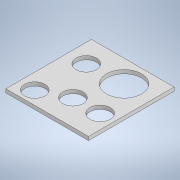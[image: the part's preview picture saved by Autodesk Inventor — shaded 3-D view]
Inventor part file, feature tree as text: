
AUTODESK INVENTOR PART (.ipt)
format: ipt  version: 2021 (Build 250183000, 183)  size: 131,584 bytes
history: native  units: mm
features: extrude x2, sketch x2
ambient origin geometry x8: Origin, YZ Plane, XZ Plane, XY Plane, X Axis, Y Axis, Z Axis, Center Point
bodies: Solid1 (feature_tree)
feature tree (4):
  extrude  "Extrusion1"  Depth=116.5mm
  extrude  "Extrusion2"  Depth=5.0mm
  sketch  "Sketch1"  dims[d0=112.5mm d1=116.5mm]
  sketch  "Sketch2"  dims[d2=5.0mm d3=0.0mm d4=47.7mm d5=27.7mm d6=27.7mm d7=27.7mm d8=27.7mm d9=116.5mm d10=112.5mm d13=37.0mm d14=18.5mm d15=30.9mm d16=5.0mm d17=0.0mm d18=18.0mm d19=35.0mm d20=35.0mm]
